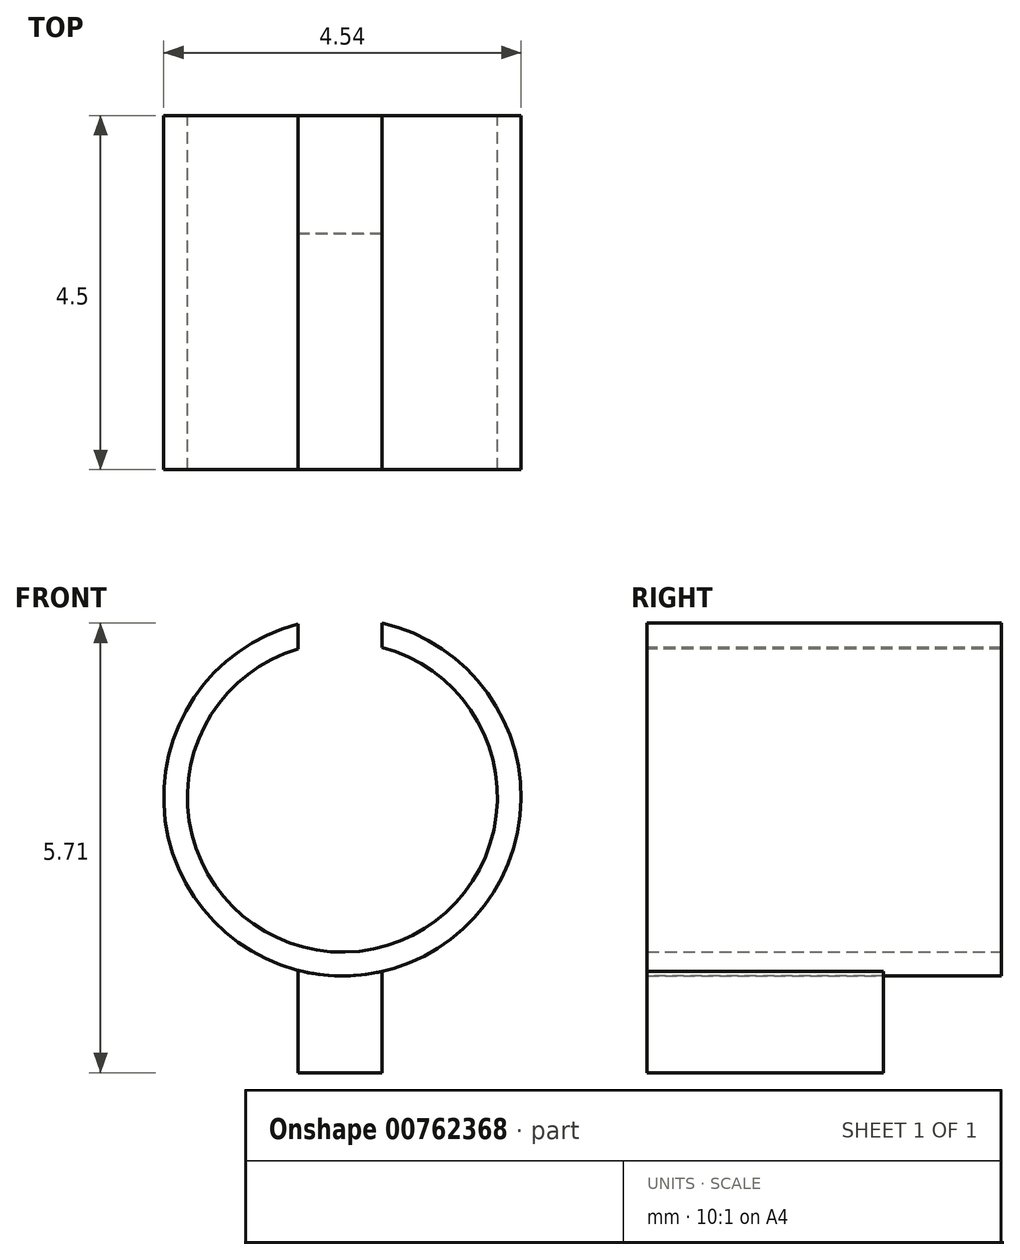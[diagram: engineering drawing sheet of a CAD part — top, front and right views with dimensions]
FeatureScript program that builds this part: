
annotation { "Feature Type Name" : "Feature", "Feature Type Description" : "" }
export const myFeature = defineFeature(function(context is Context, id is Id, definition is map)
    precondition{}
    {
        {
            var Q0;
            Q0=qCreatedBy(makeId("Front.planeOp"),FACE);
            var sketch = newSketch(context, id + "F0", { "sketchPlane" : qUnion([Q0])});
            skCircle(sketch, "E0", {"center": v(0, 0) * mm, "radius": 2.27 * mm});
            skCircle(sketch, "E1", {"center": v(0, 0) * mm, "radius": 1.97 * mm});
            skSolve(sketch);
        }
        {
            var Q0;
            Q0 = qSketchRegion(id + "F0", true);
            extrude(context, id + "F1", {"entities" : qUnion([Q0]), "depth" : 4.5 * mm, "offsetDistance" : 25 * mm});
        }
        {
            var Q0;
            Q0=makeQuery(id+"F1.opExtrude","CAP_FACE",FACE,{"disambiguationData":[OSD([sQuery(id+"F0.wireOp",EDGE,"E0"),sQuery(id+"F0.wireOp",EDGE,"E1")])],"isStart":false});
            var sketch = newSketch(context, id + "F2", { "sketchPlane" : qUnion([Q0])});
            skLineSegment(sketch, "E2", {"start": v(-0.57, 2.2) * mm, "end": v(-0.57, 1.89) * mm});
            skLineSegment(sketch, "E3", {"start": v(0.5, 2.21) * mm, "end": v(0.5, 1.9) * mm});
            skLineSegment(sketch, "E4", {"start": v(0.5, 1.9) * mm, "end": v(-0.57, 1.89) * mm});
            skArc(sketch, "E5", {"start": v(0.5, 2.21) * mm, "mid": v(-0.04, 2.75) * mm, "end": v(-0.57, 2.2) * mm});
            skSolve(sketch);
        }
        {
            var Q0;
            Q0 = qSketchRegion(id + "F2", true);
            extrude(context, id + "F3", {"entities" : qUnion([Q0]), "operationType" : NewBodyOperationType.REMOVE, "oppositeDirection" : true, "depth" : 25 * mm, "offsetDistance" : 25 * mm});
        }
        {
            var Q0;
            Q0=makeQuery(id+"F1.opExtrude","CAP_FACE",FACE,{"disambiguationData":[OSD([sQuery(id+"F0.wireOp",EDGE,"E0"),sQuery(id+"F0.wireOp",EDGE,"E1")])],"isStart":false});
            var sketch = newSketch(context, id + "F4", { "sketchPlane" : qUnion([Q0])});
            skLineSegment(sketch, "E6", {"start": v(-0.57, -2.2) * mm, "end": v(-0.57, -3.5) * mm});
            skLineSegment(sketch, "E7", {"start": v(0.5, -2.21) * mm, "end": v(0.5, -3.5) * mm});
            skLineSegment(sketch, "E8", {"start": v(0.5, -3.5) * mm, "end": v(0.5, -2.21) * mm});
            skLineSegment(sketch, "E9", {"start": v(-0.57, -3.5) * mm, "end": v(-0.57, -2.2) * mm});
            skLineSegment(sketch, "E10", {"start": v(0.5, -3.5) * mm, "end": v(-0.57, -3.5) * mm});
            skArc(sketch, "E11", {"start": v(-0.57, -2.2) * mm, "mid": v(-0.03, -2.27) * mm, "end": v(0.5, -2.21) * mm});
            skSolve(sketch);
        }
        {
            var Q0;
            Q0 = qSketchRegion(id + "F4", true);
            extrude(context, id + "F5", {"entities" : qUnion([Q0]), "oppositeDirection" : true, "depth" : 3 * mm, "offsetDistance" : 25 * mm});
        }
    });
